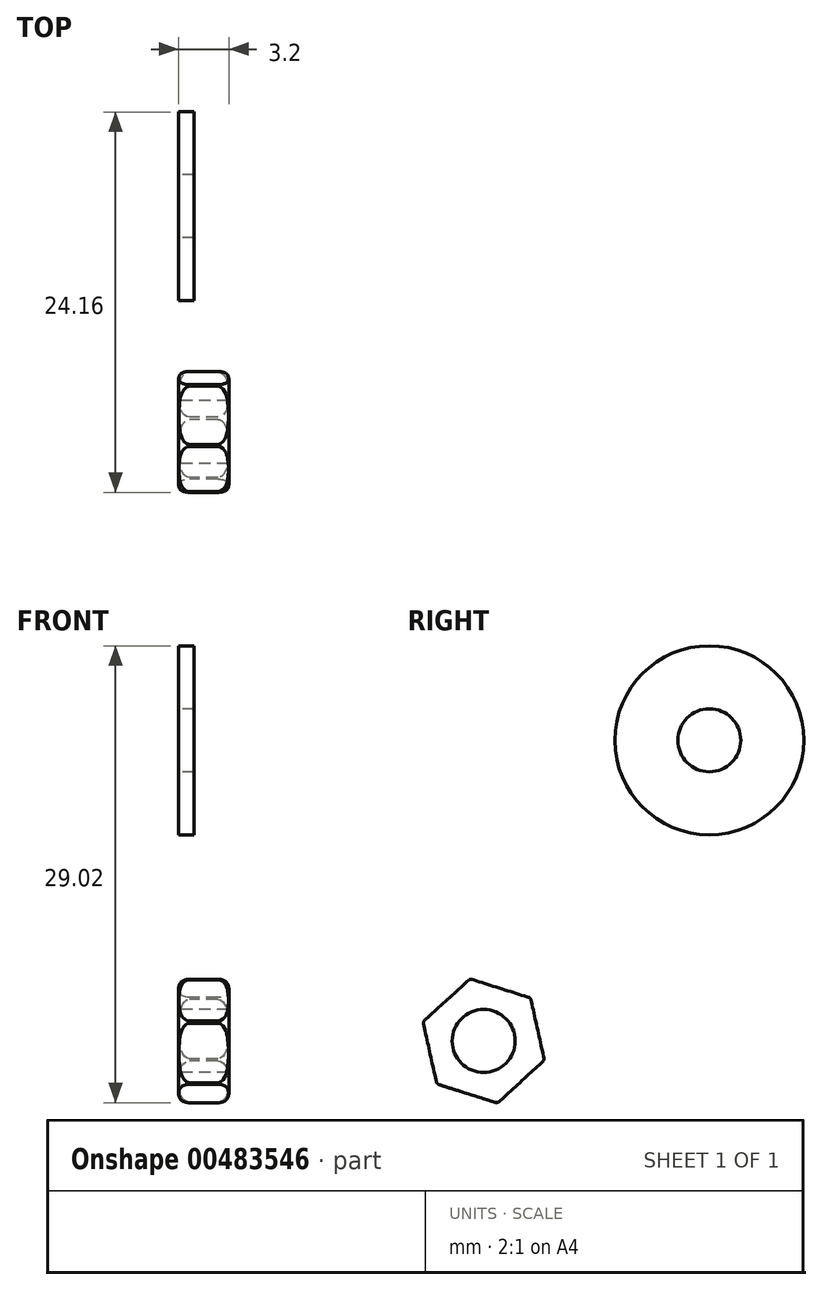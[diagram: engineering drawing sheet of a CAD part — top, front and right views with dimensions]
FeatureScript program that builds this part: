
annotation { "Feature Type Name" : "Feature", "Feature Type Description" : "" }
export const myFeature = defineFeature(function(context is Context, id is Id, definition is map)
    precondition{}
    {
        {
            var Q0;
            Q0=qCreatedBy(makeId("Front.planeOp"),FACE);
            var sketch = newSketch(context, id + "F0", { "sketchPlane" : qUnion([Q0])});
            skLineSegment(sketch, "E0", {"start": v(0, 0) * mm, "end": v(0, 3.5) * mm});
            skLineSegment(sketch, "E1", {"start": v(0, 3.5) * mm, "end": v(2.8, 3.5) * mm});
            skLineSegment(sketch, "E2", {"start": v(2.8, 3.5) * mm, "end": v(2.8, 2) * mm});
            skLineSegment(sketch, "E3", {"start": v(2.8, 2) * mm, "end": v(12.8, 2) * mm});
            skLineSegment(sketch, "E4", {"start": v(12.8, 2) * mm, "end": v(12.8, 0) * mm});
            skLineSegment(sketch, "E5", {"start": v(12.8, 0) * mm, "end": v(0, 0) * mm});
            skSolve(sketch);
        }
        {
            var Q0;
            Q0=qSketchRegion(id+"F0",true);
            var Q1;
            Q1=sQuery(id+"F0.wireOp",EDGE,"E5");
            revolve(context, id + "F1", {"entities" : qUnion([Q0]), "axis" : qUnion([Q1]), "revolveType" : RevolveType.FULL});
        }
        {
            var Q0;
            Q0=makeQuery(id+"F1.opRevolve","SWEPT_FACE",FACE,{"disambiguationData":[OSD([sQuery(id+"F0.wireOp",EDGE,"E0")])]});
            var sketch = newSketch(context, id + "F2", { "sketchPlane" : qUnion([Q0])});
            skLineSegment(sketch, "E6.left", {"start": v(0.5, -3.46) * mm, "end": v(0.5, 3.46) * mm});
            skLineSegment(sketch, "E6.right", {"start": v(-0.5, -3.46) * mm, "end": v(-0.5, 3.46) * mm});
            skPoint(sketch, "E6.middle", {"position": v(0, 0) * mm});
            skArc(sketch, "E7", {"start": v(-0.5, -3.46) * mm, "mid": v(0, -3.5) * mm, "end": v(0.5, -3.46) * mm});
            skArc(sketch, "E8.trimOffspring", {"start": v(0.5, 3.46) * mm, "mid": v(0, 3.5) * mm, "end": v(-0.5, 3.46) * mm});
            skSolve(sketch);
        }
        {
            var Q0;
            Q0=qSketchRegion(id+"F2",true);
            extrude(context, id + "F3", {"entities" : qUnion([Q0]), "operationType" : NewBodyOperationType.REMOVE, "oppositeDirection" : true, "depth" : 1.4 * mm});
        }
        {
            var Q0;
            Q0=qCreatedBy(makeId("Right.planeOp"),FACE);
            var sketch = newSketch(context, id + "F4", { "sketchPlane" : qUnion([Q0])});
            skCircle(sketch, "E9", {"center": v(-39.12, 7.47) * mm, "radius": 4 * mm});
            skCircle(sketch, "E10", {"center": v(-39.12, 7.47) * mm, "radius": 2 * mm});
            skSolve(sketch);
        }
        {
            var Q0;
            Q0 = qSketchRegion(id + "F4", true);
            extrude(context, id + "F5", {"entities" : qUnion([Q0]), "depth" : 3.2 * mm});
        }
        {
            var Q0;
            Q0=makeQuery(id+"F5.opExtrude","CAP_EDGE",EDGE,{"disambiguationData":[OSD([sQuery(id+"F4.wireOp",EDGE,"E9")])],"isStart":false});
            var Q1;
            Q1=makeQuery(id+"F5.opExtrude","CAP_EDGE",EDGE,{"disambiguationData":[OSD([sQuery(id+"F4.wireOp",EDGE,"E9")])],"isStart":true});
            fillet(context, id + "F6", {"entities" : qUnion([Q0, Q1]), "radius" : 0.7 * mm, "tangentPropagation" : true, "allowEdgeOverflow" : false});
        }
        {
            var Q0;
            Q0=makeQuery(id+"F5.opExtrude","CAP_FACE",FACE,{"disambiguationData":[OSD([sQuery(id+"F4.wireOp",EDGE,"E9"),sQuery(id+"F4.wireOp",EDGE,"E10")])],"isStart":false});
            var sketch = newSketch(context, id + "F7", { "sketchPlane" : qUnion([Q0])});
            skCircle(sketch, "E11.cCircle", {"center": v(-39.12, 7.47) * mm, "radius": 4.04 * mm, "construction": true});
            skLineSegment(sketch, "E11.0", {"start": v(-35.26, 6.25) * mm, "end": v(-38.24, 3.52) * mm});
            skLineSegment(sketch, "E11.1", {"start": v(-38.24, 3.52) * mm, "end": v(-42.1, 4.74) * mm});
            skLineSegment(sketch, "E11.2", {"start": v(-42.1, 4.74) * mm, "end": v(-42.97, 8.68) * mm});
            skLineSegment(sketch, "E11.3", {"start": v(-42.97, 8.68) * mm, "end": v(-39.99, 11.41) * mm});
            skLineSegment(sketch, "E11.4", {"start": v(-39.99, 11.41) * mm, "end": v(-36.14, 10.2) * mm});
            skLineSegment(sketch, "E11.5", {"start": v(-36.14, 10.2) * mm, "end": v(-35.26, 6.25) * mm});
            skSolve(sketch);
        }
        {
            var Q0;
            Q0 = qSketchRegion(id + "F7", true);
            extrude(context, id + "F8", {"entities" : qUnion([Q0]), "operationType" : NewBodyOperationType.INTERSECT, "endBound" : BoundingType.THROUGH_ALL, "oppositeDirection" : true, "depth" : 25 * mm});
        }
        {
            var Q0;
            Q0=qCreatedBy(makeId("Right.planeOp"),FACE);
            var sketch = newSketch(context, id + "F9", { "sketchPlane" : qUnion([Q0])});
            skCircle(sketch, "E12", {"center": v(-24.79, 26.57) * mm, "radius": 6 * mm});
            skCircle(sketch, "E13", {"center": v(-24.79, 26.57) * mm, "radius": 2 * mm});
            skSolve(sketch);
        }
        {
            var Q0;
            Q0 = qSketchRegion(id + "F9", true);
            extrude(context, id + "F10", {"entities" : qUnion([Q0]), "depth" : 1 * mm});
        }
    });
